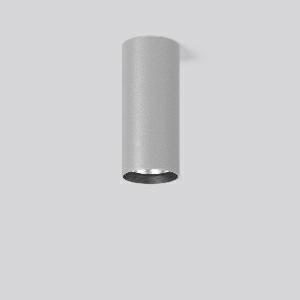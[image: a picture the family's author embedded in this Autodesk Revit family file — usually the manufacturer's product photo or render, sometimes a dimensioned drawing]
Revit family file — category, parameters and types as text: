
# Revit family: heledon_mini_a_931209_004_8b9d
name_source: partatom
category: Lighting Fixtures
units: mm (PartAtom-declared; Revit-internal decimal feet)

## family parameters
Cut with Voids When Loaded = No
Host = Face
Light Source = No
Part Type = Normal
Room Calculation Point = No
Round Connector Dimension = Use Diameter
Shared = No

## types (1)
- HELEDON mini A (1 x LED Modul 930, 3500 lm, 3000)
    Apparent Load = 29 VA
    Approval mark = CE
    CIE Flux Codes = 99 100 100 100 100
    Color Rendering = 90
    Color Temperature = 3000
    Default Elevation = 1800 mm
    Description = Series: HELEDON mini
Cylindrical surface-mounted downlight. Housing: die-cast aluminium, powder-coated. Internal ceiling frame polycarbonate with bayonet mounting. Black plastic ring and recessed LED to prevent glare from the side. Optical assembly with reflector made of MIRO-Silver with 98% total light reflection for outstanding efficiency - can be changed without tools. Best colour rendering index Ra>90. Suitable for Ceiling mounting. Easy installation with a separate ceiling frame with bayonet mounting and plug connection. Driver integrated. Connected via plug-in connector. High quality converter without flickering and stroboscopic effect. The following accessories can be mounted without use of tools: interchangeable lenses, decorative glasses, honeycomb louvre, clear and frosted diffusers, white interchangeable plastic ring. 
Colour: silver
Diameter: 87 mm
Height: 197 mm
Lamp: LED
Socket: without socket
Colour temperature: 3000K
Colour rendering index (CRI): 92
System power: 29 W
Rated luminous flux: 3500 lm
Luminous efficiency: 121 lm/W
Control gear: Regulated power supply
Protection class: I
Type of protection: IP 20
    Height = 197 mm
    Lamp = 1 x LED Modul 930
    Lamp Light Flux = 3500 lm
    Lamp count = 1
    Length = 87 mm
    Lifetime = 50000 h
    Luminous efficacy = 121 lm/W
    Manufacturer = RZB
    ModVariant = No
    Model = 931209.004
    Mounting Place = Ceiling
    Mounting Type = Surface mounted
    Number of Poles = 1
    OnlyDefault = Yes
    Power Factor = 1
    Product Name = HELEDON mini A
    Product group = Surface mounted downlights
    ProductGroupID = 302
    Protection Class = Protection class I
    Protection Degree = IP 20
    RLX_Detail_Level = 1
    RLX_Emergency_Light_Flux = 0 lm
    RLX_Emergency_Type = 0
    RLX_Emergency_Type_DB = No
    RlxData = <blob elided: 109145 chars, md5=2e6fe0b9>
    Socket = socket
    Standby Power = 0 W
    System Light Flux = 3500 lm
    System Power = 29 W
    Type Comments = Product without accessories
    Type Image = 931188.004.jpg
    URL = http://relux.com
    VarID = ---
    Voltage = 230 V
    Voltage Range = 220-240 V
    Weight = 0.00 kg
    Width = 0 mm  [stored 0 ft]

note: [stored X ft] marks values corroborated as IEEE doubles in the binary element streams (Revit-internal decimal feet)

## geometry (parser evidence)
native form markers: Blend x4, Sweep x8
no freeform markers — native parametric forms only
